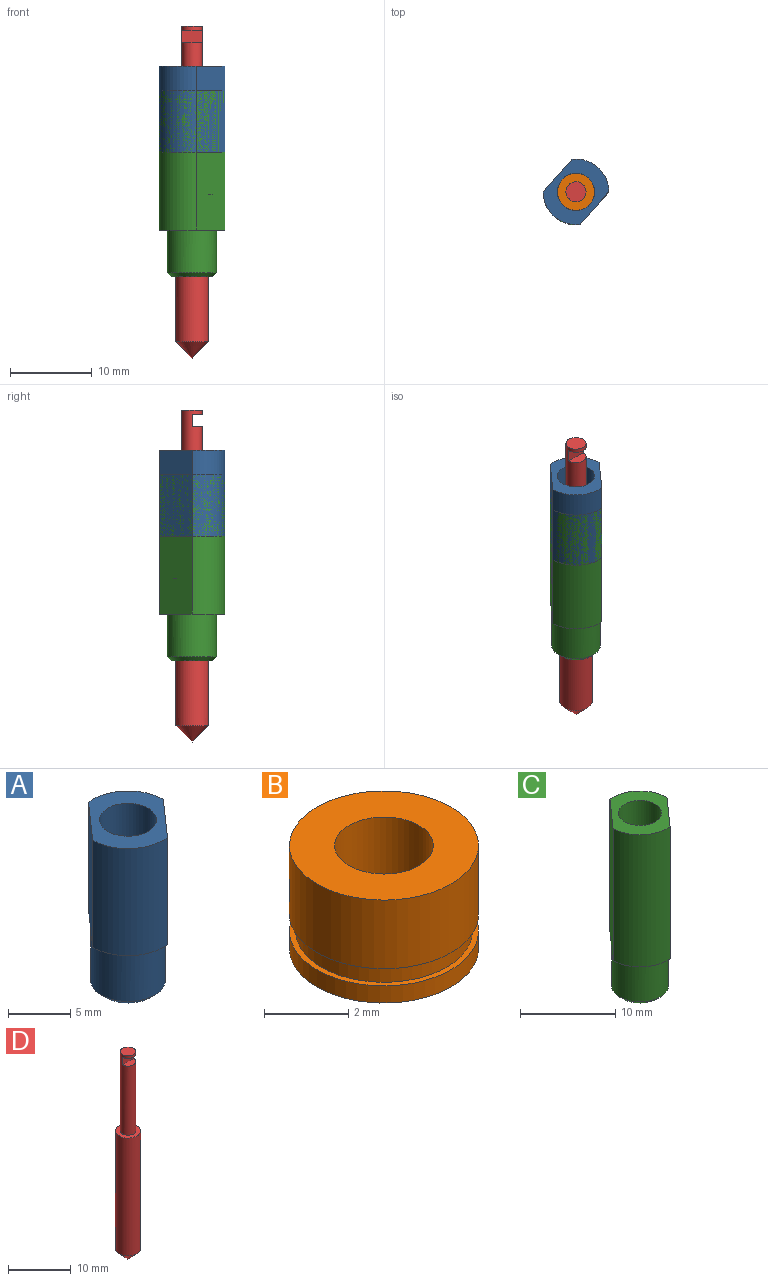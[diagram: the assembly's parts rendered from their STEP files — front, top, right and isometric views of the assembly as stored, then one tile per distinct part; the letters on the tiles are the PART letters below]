
ASSEMBLY  parts=4 mates=3
PART A: 11 faces, bbox 8x8x16.2 mm
  f0: cylinder r=4mm len=10.5mm, axis (0,0,-1), area 71.2mm2, adj f1,f2,f9,f10
  f1: plane 8x8mm, normal (0,0,1), area 26.8mm2, adj f0,f4,f5,f9,f10
  f2: plane 8x8mm, normal (0,0,-1), area 14.8mm2, adj f0,f5,f7,f9,f10
  f3: plane 4.99x4.99mm, normal (0,0,-1), area 3.3mm2, adj f4,f6
  f4: cylinder r=2.27mm len=10.5mm, axis (0,0,-1), area 150.1mm2, adj f1,f3
  f5: cylinder r=4mm len=10.5mm, axis (0,0,-1), area 71.2mm2, adj f1,f2,f9,f10
  f6: cylinder r=2.49mm len=5.7mm, axis (0,0,1), area 89.4mm2, adj f3,f8
  f7: cylinder r=2.99mm len=5.99mm, axis (0,0,1), area 97.9mm2, adj f2,f8
  f8: cone r=2.19mm half-angle=45deg, axis (0,0,1), area 12.2mm2, adj f6,f7
  f9: plane 10.5x3.97mm, normal (0.75,-0.66,0), area 55.6mm2, adj f0,f1,f2,f5
  f10: plane 10.5x3.97mm, normal (-0.75,0.66,0), area 55.6mm2, adj f0,f1,f2,f5
PART B: 8 faces, bbox 4.5x4.5x3 mm
  f0: cylinder r=1.18mm len=3mm, axis (0,0,-1), area 22.1mm2, adj f2,f6
  f1: cylinder r=2.25mm len=4.5mm, axis (0,0,-1), area 28.3mm2, adj f2,f3
  f2: plane 4.5x4.5mm, normal (0,0,1), area 11.6mm2, adj f0,f1
  f3: plane 4.5x4.5mm, normal (0,0,-1), area 2mm2, adj f1,f4
  f4: cylinder r=2.1mm len=4.2mm, axis (0,0,1), area 6.6mm2, adj f3,f7
  f5: cylinder r=2.25mm len=4.5mm, axis (0,0,1), area 7.1mm2, adj f6,f7
  f6: plane 4.5x4.5mm, normal (0,0,-1), area 11.6mm2, adj f0,f5
  f7: plane 4.5x4.5mm, normal (0,0,1), area 2mm2, adj f4,f5
PART C: 11 faces, bbox 8x8x22.7 mm
  f0: cylinder r=4mm len=17mm, axis (0,0,-1), area 115.3mm2, adj f1,f2,f9,f10
  f1: plane 8x8mm, normal (0,0,1), area 26.8mm2, adj f0,f4,f5,f9,f10
  f2: plane 8x8mm, normal (0,0,-1), area 14.8mm2, adj f0,f5,f7,f9,f10
  f3: plane 4.99x4.99mm, normal (0,0,-1), area 3.3mm2, adj f4,f6
  f4: cylinder r=2.27mm len=17mm, axis (0,0,-1), area 243mm2, adj f1,f3
  f5: cylinder r=4mm len=17mm, axis (0,0,-1), area 115.3mm2, adj f1,f2,f9,f10
  f6: cylinder r=2.49mm len=5.7mm, axis (0,0,1), area 89.4mm2, adj f3,f8
  f7: cylinder r=2.99mm len=5.99mm, axis (0,0,1), area 97.9mm2, adj f2,f8
  f8: cone r=2.19mm half-angle=45deg, axis (0,0,1), area 12.2mm2, adj f6,f7
  f9: plane 17x3.97mm, normal (0.75,-0.66,0), area 90mm2, adj f0,f1,f2,f5
  f10: plane 17x3.97mm, normal (-0.75,0.66,0), area 90mm2, adj f0,f1,f2,f5
PART D: 8 faces, bbox 4x4x40.5 mm
  f0: cylinder r=1.22mm len=15.5mm, axis (0,0,-1), area 113.5mm2, adj f1,f3,f5,f6,f7
  f1: plane 2.45x1.23mm, normal (0,0,1), area 2.4mm2, adj f0,f5
  f2: cylinder r=2mm len=23mm, axis (0,0,1), area 289mm2, adj f3,f4
  f3: plane 4x4mm, normal (0,0,1), area 7.9mm2, adj f0,f2
  f4: cone r=2mm half-angle=45deg, axis (0,0,1), area 17.8mm2, adj f2
  f5: plane 2.45x1.5mm, normal (0,-1,0), area 3.7mm2, adj f0,f1,f6
  f6: plane 2.45x1.23mm, normal (0,0,-1), area 2.4mm2, adj f0,f5
  f7: plane 2.45x2.45mm, normal (0,0,1), area 4.7mm2, adj f0
PLACE A t=(-4.25,-5.3,0.74)mm
PLACE B t=(-4.25,-5.3,6.24)mm
PLACE C t=(-4.25,-5.3,-8.76)mm
PLACE D t=(-4.25,-5.3,0.62)mm
MATE slider C.f4 <-> B.f1  axis (0,0,-1) through (-4.25,-5.3,8.24)mm
MATE planar C.f1 <-> B.f1  axis (0,0,1) through (-3.75,-9.27,8.24)mm
MATE slider B.f0 <-> D.f0  axis (0,0,-1) through (-4.25,-5.3,8.24)mm
